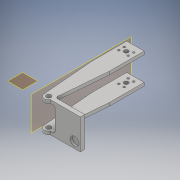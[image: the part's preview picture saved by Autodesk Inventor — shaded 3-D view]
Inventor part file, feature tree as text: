
AUTODESK INVENTOR PART (.ipt)
format: ipt  version: 2017 (Build 210142000, 142)  size: 269,312 bytes
history: native  units: in
note: dims shown in document units (in); Inventor stores cm internally (conversion verified against a paired STEP export)
features: sketch x9, projected_geometry x9, hole x5, extrude x4, plane x3, fillet x2, mirror x1
ambient origin geometry x8: Origin, YZ Plane, XZ Plane, XY Plane, X Axis, Y Axis, Z Axis, Center Point
bodies: Solid1 (feature_tree)
feature tree (33):
  sketch  "Sketch1"  dims[d0=5.0in d1=1.0in]
  plane  "Work Plane1"
  extrude  "Extrusion2"  Depth=1.0in
  plane  "Work Plane2"
  extrude  "Extrusion3"  Depth=1.0in
  hole  "Hole2"  [1 undecoded]
  extrude  "Extrusion4"  Depth=1.753in
  extrude  "Extrusion5"  Depth=1.753in
  fillet  "Fillet1"  Radius=2.0in
  fillet  "Fillet2"  Radius=1.753in
  hole  "Hole3"  [1 undecoded]
  hole  "Hole4"  [1 undecoded]
  hole  "Hole5"  [1 undecoded]
  hole  "Hole6"  [1 undecoded]
  plane  "Work Plane3"
  mirror  "Mirror1"
  sketch  "Sketch2"  dims[d5=1.0in d6=0.5in]
  projected_geometry  "Projected Loop1"
  sketch  "Sketch4"  dims[d7=0.5in d8=0.0in]
  projected_geometry  "Projected Loop3"
  sketch  "Sketch5"  dims[d9=1.753in d10=0.0in d18=0.5in]
  projected_geometry  "Projected Loop4"
  sketch  "Sketch8"  dims[d19=0.25in d20=2.0in d21=2.0in d22=1.753in d23=0.0in]
  projected_geometry  "Projected Loop9"
  projected_geometry  "Projected Loop10"
  sketch  "Sketch9"  dims[d24=0.27in d25=0.75in d26=0.375in d27=0.25in d28=0.5635in d29=1.0in d30=0.8108in d31=1.75in]
  projected_geometry  "Projected Loop11"
  sketch  "Sketch10"  dims[d32=0.25in d35=5.0in]
  projected_geometry  "Projected Loop12"
  sketch  "Sketch11"  dims[d36=4.875in d37=1.753in d38=0.0in]
  projected_geometry  "Projected Loop13"
  sketch  "Sketch12"  dims[d41=1.753in d42=5.375in d43=1.378in d44=0.1875in d45=5.875in d46=1.0in d47=0.0in d48=0.125in d49=0.125in d50=0.6299in d51=1.0in d52=0.5in d55=0.117in d56=0.75in d57=0.375in d58=0.25in d59=0.5635in d60=1.0in d61=0.8108in d62=0.6299in d63=1.0in d64=0.5in d67=0.117in d68=0.75in d69=0.375in d70=0.25in d71=0.5635in d72=1.0in d73=0.8108in d74=0.32in d75=1.753in d77=0.5in d78=0.75in d79=0.375in d80=0.25in d81=0.5635in d82=0.125in d83=0.0in d84=1.0in d85=0.5in d86=0.315in d87=0.1575in d88=0.25in d89=0.75in d90=0.375in d91=0.25in d92=0.5635in d93=1.0in d94=0.8108in d95=0.27in d96=0.1975in d97=0.375in d98=0.315in d99=0.1575in d100=0.53in d101=0.315in d102=0.1575in d103=0.53in]
  projected_geometry  "Projected Loop14"
note: 5 required parameter values undecoded (feature->parameter linkage not recoverable at this tier; creation-order binding heuristic only, values carry confidence <= 0.55)
